# Revit family: MFJ-48ARN1-R
name_source: partatom
category: Mechanical Equipment
revit_build: Autodesk Revit 2013 (Build: 20120221_2030(x64)
units: mm (PartAtom-declared; Revit-internal decimal feet)

## types (1)
- MFJ-48ARN1-R
    Air  Flow = 1488/1180 m3/h
    Combine = 3700 W
    Combine Capacity = 3517 W
    Cooling Capacity = 14068 W
    Cooling Power Input = 5300 W
    Depth = 410 mm  [stored 1.34514 ft]
    Description = Floor standing
    Gas = R410A
    Gas pipe = 19 mm  [stored 0.062336 ft]
    Heating Capacity = 16120 W
    Heating Power Input = 5300 W
    Height = 1825 mm  [stored 5.98753 ft]
    Installation = Indoor installation
    Liquid pipe = 9.52 mm
    Machine material = Galvanized Steel
    Maximum Fuse Amps = 15 A
    Min cable selection (power wiring) = 2.5x5
    Minimum Circuit Amps = 11 A
    Model = MFJ-48ARN1-R
    Net Weight = 52.90 kg
    Panel color = Polar white
    Power supply = 3 phase,380-415V, 50Hz
    Series = J2
    Width = 540 mm  [stored 1.77165 ft]
    clearance access behind = 50 mm  [stored 0.164042 ft]
    clearance access front = 2000 mm  [stored 6.56168 ft]
    clearance access left = 500 mm  [stored 1.64042 ft]
    clearance access right = 500 mm  [stored 1.64042 ft]
    clearance access up = 300 mm

note: [stored X ft] marks values corroborated as IEEE doubles in the binary element streams (Revit-internal decimal feet)

## geometry (parser evidence)
native form markers: Sweep x2
no freeform markers — native parametric forms only
